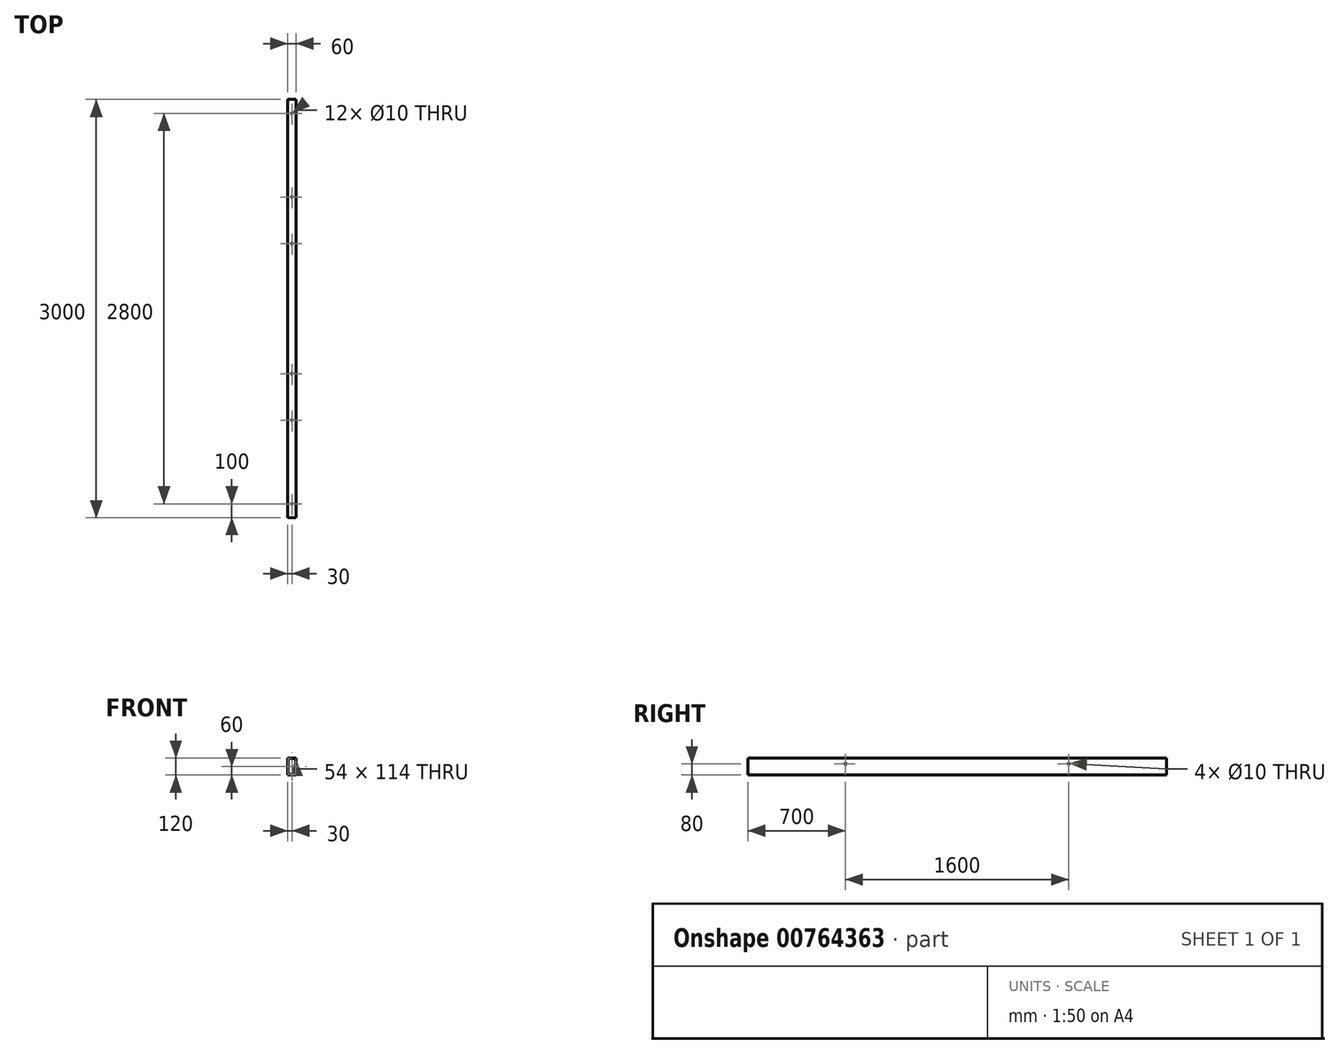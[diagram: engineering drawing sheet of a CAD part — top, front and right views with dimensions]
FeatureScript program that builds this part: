
annotation { "Feature Type Name" : "Feature", "Feature Type Description" : "" }
export const myFeature = defineFeature(function(context is Context, id is Id, definition is map)
    precondition{}
    {
        {
            var Q0;
            Q0=qCreatedBy(makeId("Front.planeOp"),FACE);
            var sketch = newSketch(context, id + "F0", { "sketchPlane" : qUnion([Q0])});
            skLineSegment(sketch, "E0", {"start": v(-30, 0) * mm, "end": v(-30, 60) * mm});
            skLineSegment(sketch, "E1", {"start": v(-30, 60) * mm, "end": v(30, 60) * mm});
            skLineSegment(sketch, "E2", {"start": v(30, 60) * mm, "end": v(30, -60) * mm});
            skLineSegment(sketch, "E3", {"start": v(30, -60) * mm, "end": v(-30, -60) * mm});
            skLineSegment(sketch, "E4", {"start": v(-30, -60) * mm, "end": v(-30, 0) * mm});
            skLineSegment(sketch, "E5.0", {"start": v(-27, 57) * mm, "end": v(27, 57) * mm});
            skLineSegment(sketch, "E5.1", {"start": v(-27, 0) * mm, "end": v(-27, 57) * mm});
            skLineSegment(sketch, "E5.2", {"start": v(27, 57) * mm, "end": v(27, -57) * mm});
            skLineSegment(sketch, "E5.3", {"start": v(27, -57) * mm, "end": v(-27, -57) * mm});
            skLineSegment(sketch, "E5.4", {"start": v(-27, -57) * mm, "end": v(-27, 0) * mm});
            skSolve(sketch);
        }
        {
            var Q0;
            Q0=makeQuery(id+"F0.imprint","IMPRINT",FACE,{"disambiguationData":[TD([[makeQuery(id+"F0.imprint","IMPRINT",EDGE,{"derivedFrom":sQuery(id+"F0.wireOp",EDGE,"E0")}),-1.0]])]});
            extrude(context, id + "F1", {"entities" : qUnion([Q0]), "depth" : 3000 * mm, "offsetDistance" : 25 * mm, "symmetric" : true});
        }
        {
            var Q0;
            Q0=makeQuery(id+"F1.opExtrude","SWEPT_FACE",FACE,{"disambiguationData":[OSD([sQuery(id+"F0.wireOp",EDGE,"E1")])]});
            var sketch = newSketch(context, id + "F2", { "sketchPlane" : qUnion([Q0])});
            skCircle(sketch, "E6", {"center": v(0, -800) * mm, "radius": 5 * mm});
            skPoint(sketch, "E6.centerSnap0", {"position": v(0, -1500) * mm});
            skCircle(sketch, "E7", {"center": v(0, 800) * mm, "radius": 5 * mm});
            skPoint(sketch, "E7.centerSnap0", {"position": v(0, 1500) * mm});
            skCircle(sketch, "E8", {"center": v(0, -1400) * mm, "radius": 5 * mm});
            skCircle(sketch, "E9", {"center": v(0, 1400) * mm, "radius": 5 * mm});
            skCircle(sketch, "E10", {"center": v(0, -467) * mm, "radius": 5 * mm});
            skCircle(sketch, "E11", {"center": v(0, 466) * mm, "radius": 5 * mm});
            skSolve(sketch);
        }
        {
            var Q0;
            Q0=sQuery(id+"F2.wireOp",VERTEX,"E7.center");
            var Q1;
            Q1=sQuery(id+"F2.wireOp",VERTEX,"E6.center");
            var Q2;
            Q2=sQuery(id+"F2.wireOp",VERTEX,"E9.center");
            var Q3;
            Q3=sQuery(id+"F2.wireOp",VERTEX,"E11.center");
            var Q4;
            Q4=sQuery(id+"F2.wireOp",VERTEX,"E10.center");
            var Q5;
            Q5=sQuery(id+"F2.wireOp",VERTEX,"E8.center");
            var Q6;
            Q6=makeQuery(id+"F1.opExtrude","SWEPT_BODY",BODY,{"disambiguationData":[OSD([sQuery(id+"F0.wireOp",EDGE,"E0"),sQuery(id+"F0.wireOp",EDGE,"E1"),sQuery(id+"F0.wireOp",EDGE,"E2"),sQuery(id+"F0.wireOp",EDGE,"E3"),sQuery(id+"F0.wireOp",EDGE,"E4"),sQuery(id+"F0.wireOp",EDGE,"E5.0"),sQuery(id+"F0.wireOp",EDGE,"E5.1"),sQuery(id+"F0.wireOp",EDGE,"E5.2"),sQuery(id+"F0.wireOp",EDGE,"E5.3"),sQuery(id+"F0.wireOp",EDGE,"E5.4")])]});
            hole(context, id + "F3", {"style" : HoleStyle.SIMPLE, "endStyle" : HoleEndStyle.THROUGH, "holeDiameter" : 10 * mm, "majorDiameter" : 5 * mm, "isTappedThrough" : true, "tappedDepth" : 12 * mm, "tapClearance" : 3, "locations" : qUnion([Q0, Q1, Q2, Q3, Q4, Q5]), "scope" : qUnion([Q6]), "startStyle" : HoleStartStyle.PART});
        }
        {
            var Q0;
            Q0=makeQuery(id+"F1.opExtrude","SWEPT_FACE",FACE,{"disambiguationData":[OSD([sQuery(id+"F0.wireOp",EDGE,"E0"),sQuery(id+"F0.wireOp",EDGE,"E4")])]});
            var sketch = newSketch(context, id + "F4", { "sketchPlane" : qUnion([Q0])});
            skPoint(sketch, "E12.centerSnap0", {"position": v(1500, 0) * mm});
            skCircle(sketch, "E13", {"center": v(800, 20) * mm, "radius": 5 * mm});
            skCircle(sketch, "E14", {"center": v(-800, 20) * mm, "radius": 5 * mm});
            skSolve(sketch);
        }
        {
            var Q0;
            Q0=sQuery(id+"F4.wireOp",VERTEX,"E14.center");
            var Q1;
            Q1=sQuery(id+"F4.wireOp",VERTEX,"E13.center");
            var Q2;
            Q2=makeQuery(id+"F1.opExtrude","SWEPT_BODY",BODY,{"disambiguationData":[OSD([sQuery(id+"F0.wireOp",EDGE,"E0"),sQuery(id+"F0.wireOp",EDGE,"E1"),sQuery(id+"F0.wireOp",EDGE,"E2"),sQuery(id+"F0.wireOp",EDGE,"E3"),sQuery(id+"F0.wireOp",EDGE,"E4"),sQuery(id+"F0.wireOp",EDGE,"E5.0"),sQuery(id+"F0.wireOp",EDGE,"E5.1"),sQuery(id+"F0.wireOp",EDGE,"E5.2"),sQuery(id+"F0.wireOp",EDGE,"E5.3"),sQuery(id+"F0.wireOp",EDGE,"E5.4")])]});
            hole(context, id + "F5", {"style" : HoleStyle.SIMPLE, "endStyle" : HoleEndStyle.THROUGH, "holeDiameter" : 10 * mm, "majorDiameter" : 5 * mm, "isTappedThrough" : true, "tappedDepth" : 12 * mm, "tapClearance" : 3, "locations" : qUnion([Q0, Q1]), "scope" : qUnion([Q2]), "startStyle" : HoleStartStyle.PART});
        }
    });
